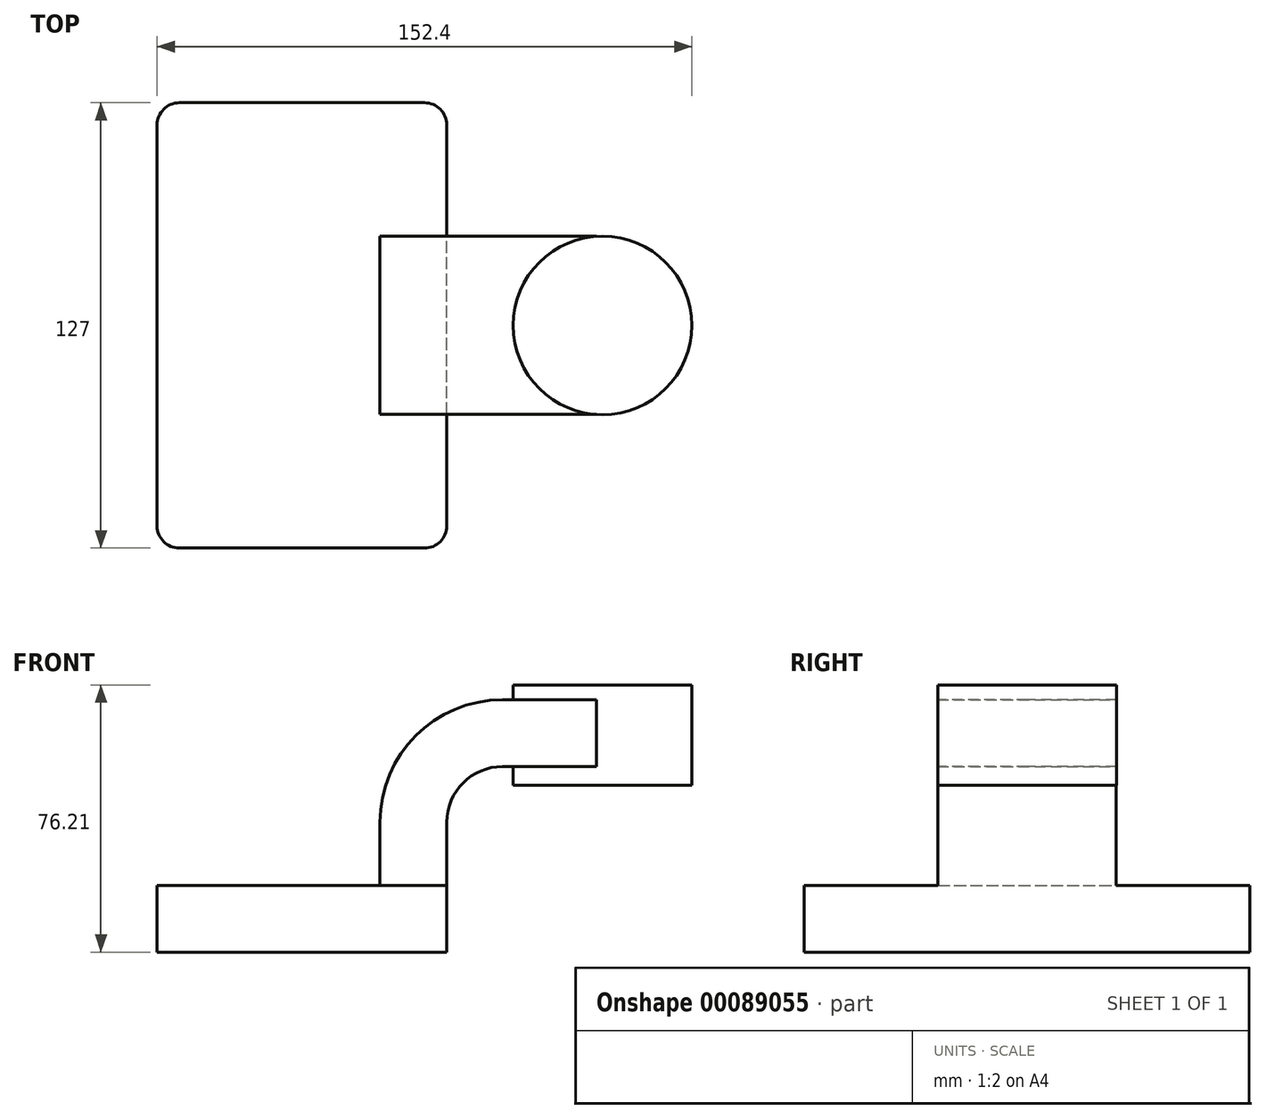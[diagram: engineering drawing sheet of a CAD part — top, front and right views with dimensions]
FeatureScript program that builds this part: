
annotation { "Feature Type Name" : "Feature", "Feature Type Description" : "" }
export const myFeature = defineFeature(function(context is Context, id is Id, definition is map)
    precondition{}
    {
        {
            var Q0;
            Q0=qCreatedBy(makeId("Front.planeOp"),FACE);
            var sketch = newSketch(context, id + "F0", { "sketchPlane" : qUnion([Q0])});
            skLineSegment(sketch, "E0.bottom", {"start": v(41.28, -9.52) * mm, "end": v(-41.28, -9.53) * mm});
            skLineSegment(sketch, "E0.top", {"start": v(41.28, 9.53) * mm, "end": v(-41.28, 9.53) * mm});
            skLineSegment(sketch, "E0.left", {"start": v(41.28, -9.52) * mm, "end": v(41.28, 9.53) * mm});
            skLineSegment(sketch, "E0.right", {"start": v(-41.28, -9.53) * mm, "end": v(-41.28, 9.53) * mm});
            skPoint(sketch, "E0.middle", {"position": v(0, 0) * mm});
            skLineSegment(sketch, "E1.bottom", {"start": v(111.12, 38.1) * mm, "end": v(60.32, 38.1) * mm});
            skLineSegment(sketch, "E1.top", {"start": v(111.12, 66.68) * mm, "end": v(60.32, 66.68) * mm});
            skLineSegment(sketch, "E1.left", {"start": v(111.12, 38.1) * mm, "end": v(111.12, 66.68) * mm});
            skLineSegment(sketch, "E1.right", {"start": v(60.32, 38.1) * mm, "end": v(60.32, 66.67) * mm});
            skPoint(sketch, "E1.middle", {"position": v(85.72, 52.39) * mm});
            skLineSegment(sketch, "E2", {"start": v(41.28, 9.53) * mm, "end": v(41.28, 27.5) * mm});
            skArc(sketch, "E3", {"start": v(41.27, 27.5) * mm, "mid": v(45.92, 38.73) * mm, "end": v(57.15, 43.38) * mm});
            skLineSegment(sketch, "E4", {"start": v(57.15, 43.38) * mm, "end": v(85.66, 43.38) * mm});
            skLineSegment(sketch, "E5.0", {"start": v(57.15, 62.43) * mm, "end": v(85.66, 62.43) * mm});
            skArc(sketch, "E5.1", {"start": v(22.23, 27.5) * mm, "mid": v(32.45, 52.2) * mm, "end": v(57.15, 62.43) * mm});
            skLineSegment(sketch, "E5.2", {"start": v(22.22, 9.53) * mm, "end": v(22.22, 27.5) * mm});
            skFitSpline(sketch, "E6", {"points": [v(-41.28, 9.52) * mm, v(60.32, 66.67) * mm], "startDerivative": vector(-0.15, 94.44) * mm, "endDerivative": vector(149.93, 5) * mm});
            skLineSegment(sketch, "E7", {"start": v(85.66, 38.1) * mm, "end": v(85.66, 66.68) * mm});
            skSolve(sketch);
        }
        {
            var Q0;
            Q0=makeQuery(id+"F0.imprint","IMPRINT",FACE,{"disambiguationData":[TD([[makeQuery(id+"F0.imprint","IMPRINT",EDGE,{"derivedFrom":sQuery(id+"F0.wireOp",EDGE,"E0.bottom")}),-1.0]])]});
            extrude(context, id + "F1", {"entities" : qUnion([Q0]), "endBound" : BoundingType.SYMMETRIC, "depth" : 127 * mm});
        }
        {
            var Q0;
            {var subQ1=sQuery(id+"F0.wireOp",EDGE,"E2");Q0=makeQuery(id+"F0.imprint","IMPRINT",FACE,{"disambiguationData":[TD([[makeQuery(id+"F0.imprint","IMPRINT",EDGE,{"derivedFrom":subQ1}),1.0]])]});}
            var Q1;
            {var subQ0=sQuery(id+"F0.wireOp",EDGE,"E4");var subQ1=sQuery(id+"F0.wireOp",EDGE,"E1.right");var subQ2=makeQuery(id+"F0.imprint","INTERSECT",VERTEX,{"derivedFrom":[subQ1,subQ0]});Q1=makeQuery(id+"F0.imprint","IMPRINT",FACE,{"disambiguationData":[TD([[makeQuery(id+"F0.imprint","IMPRINT",EDGE,{"disambiguationData":[TD([[subQ2,-1.0]])],"derivedFrom":subQ1}),-1.0]])]});}
            extrude(context, id + "F2", {"entities" : qUnion([Q0, Q1]), "operationType" : NewBodyOperationType.ADD, "endBound" : BoundingType.SYMMETRIC, "depth" : 50.8 * mm});
        }
        {
            var Q0;
            {var subQ0=sQuery(id+"F0.wireOp",EDGE,"E5.1");Q0=makeQuery(id+"F0.imprint","IMPRINT",FACE,{"disambiguationData":[TD([[makeQuery(id+"F0.imprint","IMPRINT",EDGE,{"derivedFrom":subQ0}),1.0]])]});}
            extrude(context, id + "F3", {"entities" : qUnion([Q0]), "operationType" : NewBodyOperationType.ADD, "endBound" : BoundingType.SYMMETRIC, "depth" : 15.88 * mm});
        }
        {
            var Q0;
            {var subQ0=sQuery(id+"F0.wireOp",EDGE,"E1.left");Q0=makeQuery(id+"F0.imprint","IMPRINT",FACE,{"disambiguationData":[TD([[makeQuery(id+"F0.imprint","IMPRINT",EDGE,{"derivedFrom":subQ0}),1.0]])]});}
            var Q1;
            Q1=sQuery(id+"F0.wireOp",EDGE,"E7");
            revolve(context, id + "F4", {"operationType" : NewBodyOperationType.ADD, "entities" : qUnion([Q0]), "axis" : qUnion([Q1]), "revolveType" : RevolveType.FULL});
        }
        {
            var Q0;
            Q0=makeQuery(id+"F1.opExtrude","CAP_EDGE",EDGE,{"disambiguationData":[OSD([sQuery(id+"F0.wireOp",EDGE,"E0.left")])],"isStart":false});
            var Q1;
            Q1=makeQuery(id+"F1.opExtrude","CAP_EDGE",EDGE,{"disambiguationData":[OSD([sQuery(id+"F0.wireOp",EDGE,"E0.right")])],"isStart":false});
            var Q2;
            Q2=makeQuery(id+"F1.opExtrude","CAP_EDGE",EDGE,{"disambiguationData":[OSD([sQuery(id+"F0.wireOp",EDGE,"E0.left")])],"isStart":true});
            var Q3;
            Q3=makeQuery(id+"F1.opExtrude","CAP_EDGE",EDGE,{"disambiguationData":[OSD([sQuery(id+"F0.wireOp",EDGE,"E0.right")])],"isStart":true});
            fillet(context, id + "F5", {"entities" : qUnion([Q0, Q1, Q2, Q3]), "radius" : 6.35 * mm, "tangentPropagation" : true, "allowEdgeOverflow" : false});
        }
    });
